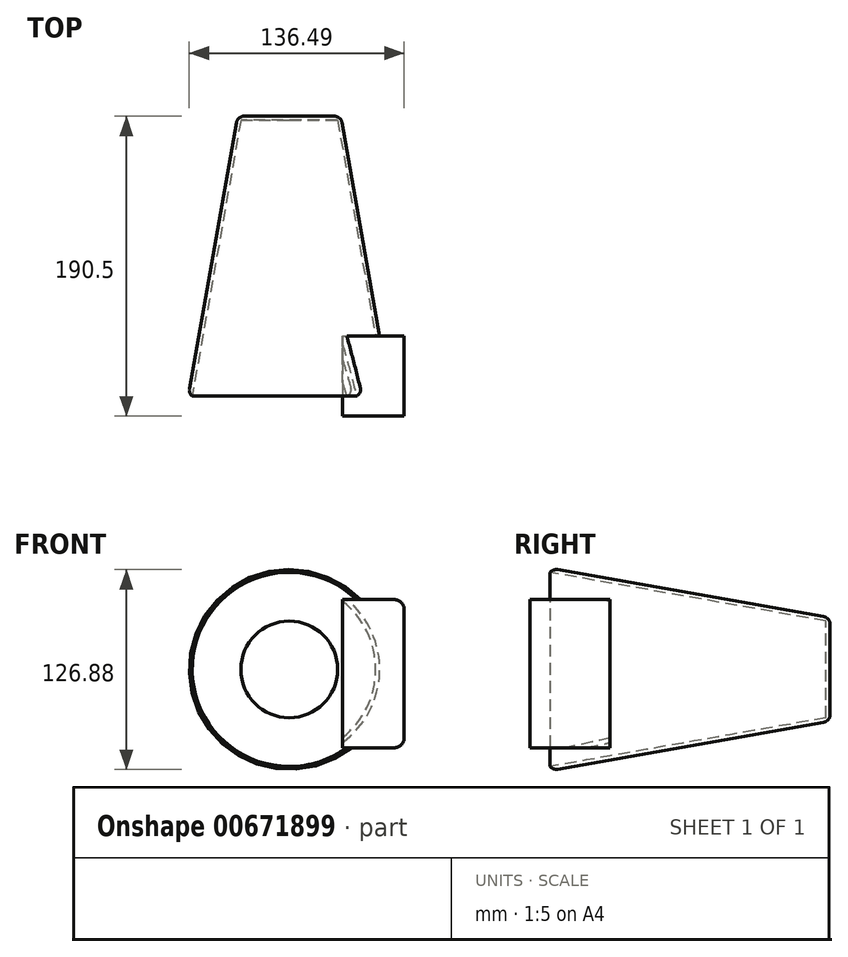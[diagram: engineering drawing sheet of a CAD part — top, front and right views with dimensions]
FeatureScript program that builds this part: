
annotation { "Feature Type Name" : "Feature", "Feature Type Description" : "" }
export const myFeature = defineFeature(function(context is Context, id is Id, definition is map)
    precondition{}
    {
        {
            var Q0;
            Q0=qCreatedBy(makeId("Front.planeOp"),FACE);
            var sketch = newSketch(context, id + "F0", { "sketchPlane" : qUnion([Q0])});
            skCircle(sketch, "E0", {"center": v(-33.84, 32.33) * mm, "radius": 32.85 * mm});
            skSolve(sketch);
        }
        {
            var Q0;
            Q0=makeQuery(id+"F0.imprint","IMPRINT",FACE,{"disambiguationData":[TD([[makeQuery(id+"F0.imprint","IMPRINT",EDGE,{"derivedFrom":sQuery(id+"F0.wireOp",EDGE,"E0")}),1.0]])]});
            extrude(context, id + "F1", {"entities" : qUnion([Q0]), "depth" : 177.8 * mm, "offsetDistance" : 25.4 * mm, "hasDraft" : true, "draftAngle" : 10 * degree});
        }
        {
            var Q0;
            Q0=makeQuery(id+"F1.opExtrude","CAP_FACE",FACE,{"disambiguationData":[OSD([sQuery(id+"F0.wireOp",EDGE,"E0")])],"isStart":false});
            var sketch = newSketch(context, id + "F2", { "sketchPlane" : qUnion([Q0])});
            skSolve(sketch);
        }
        {
            var Q0;
            Q0=makeQuery(id+"F1.opExtrude","CAP_FACE",FACE,{"disambiguationData":[OSD([sQuery(id+"F0.wireOp",EDGE,"E0")])],"isStart":false});
            shell(context, id + "F3", {"entities" : qUnion([Q0]), "thickness" : 2.54 * mm});
        }
        {
            var Q0;
            Q0=makeQuery(id+"F1.opExtrude","CAP_EDGE",EDGE,{"disambiguationData":[OSD([sQuery(id+"F0.wireOp",EDGE,"E0")])],"isStart":true});
            var Q1;
            Q1=makeQuery(id+"F1.opExtrude","CAP_EDGE",EDGE,{"disambiguationData":[OSD([sQuery(id+"F0.wireOp",EDGE,"E0")])],"isStart":false});
            fillet(context, id + "F4", {"entities" : qUnion([Q0, Q1]), "radius" : 5.08 * mm, "tangentPropagation" : true, "allowEdgeOverflow" : false});
        }
        {
            var Q0;
            Q0=qCreatedBy(makeId("Front.planeOp"),FACE);
            cPlane(context, id + "F5", {"entities" : qUnion([Q0]), "cplaneType" : CPlaneType.OFFSET, "offset" : 190.5 * mm, "width" : 152.4 * mm, "height" : 152.4 * mm});
        }
        {
            var Q0;
            Q0=qCreatedBy(id+"F5.planeOp",FACE);
            var sketch = newSketch(context, id + "F6", { "sketchPlane" : qUnion([Q0])});
            skLineSegment(sketch, "E1.bottom", {"start": v(0, -17.37) * mm, "end": v(32.86, -17.37) * mm});
            skLineSegment(sketch, "E1.top", {"start": v(0, 76.7) * mm, "end": v(32.86, 76.7) * mm});
            skLineSegment(sketch, "E1.left", {"start": v(0, -17.37) * mm, "end": v(0, 76.7) * mm});
            skLineSegment(sketch, "E1.right", {"start": v(39.21, -11.02) * mm, "end": v(39.21, 70.35) * mm});
            skPoint(sketch, "E2.visualSharp", {"position": v(39.21, 76.7) * mm});
            skArc(sketch, "E2.filletArc", {"start": v(39.21, 70.35) * mm, "mid": v(37.35, 74.84) * mm, "end": v(32.86, 76.7) * mm});
            skPoint(sketch, "E3.visualSharp", {"position": v(39.21, -17.37) * mm});
            skArc(sketch, "E3.filletArc", {"start": v(32.86, -17.37) * mm, "mid": v(37.35, -15.51) * mm, "end": v(39.21, -11.02) * mm});
            skSolve(sketch);
        }
        {
            var Q0;
            Q0=makeQuery(id+"F6.imprint","IMPRINT",FACE,{"disambiguationData":[TD([[makeQuery(id+"F6.imprint","IMPRINT",EDGE,{"derivedFrom":sQuery(id+"F6.wireOp",EDGE,"E1.bottom")}),1.0]])]});
            extrude(context, id + "F7", {"entities" : qUnion([Q0]), "operationType" : NewBodyOperationType.ADD, "oppositeDirection" : true, "depth" : 50.8 * mm, "offsetDistance" : 25.4 * mm});
        }
    });
